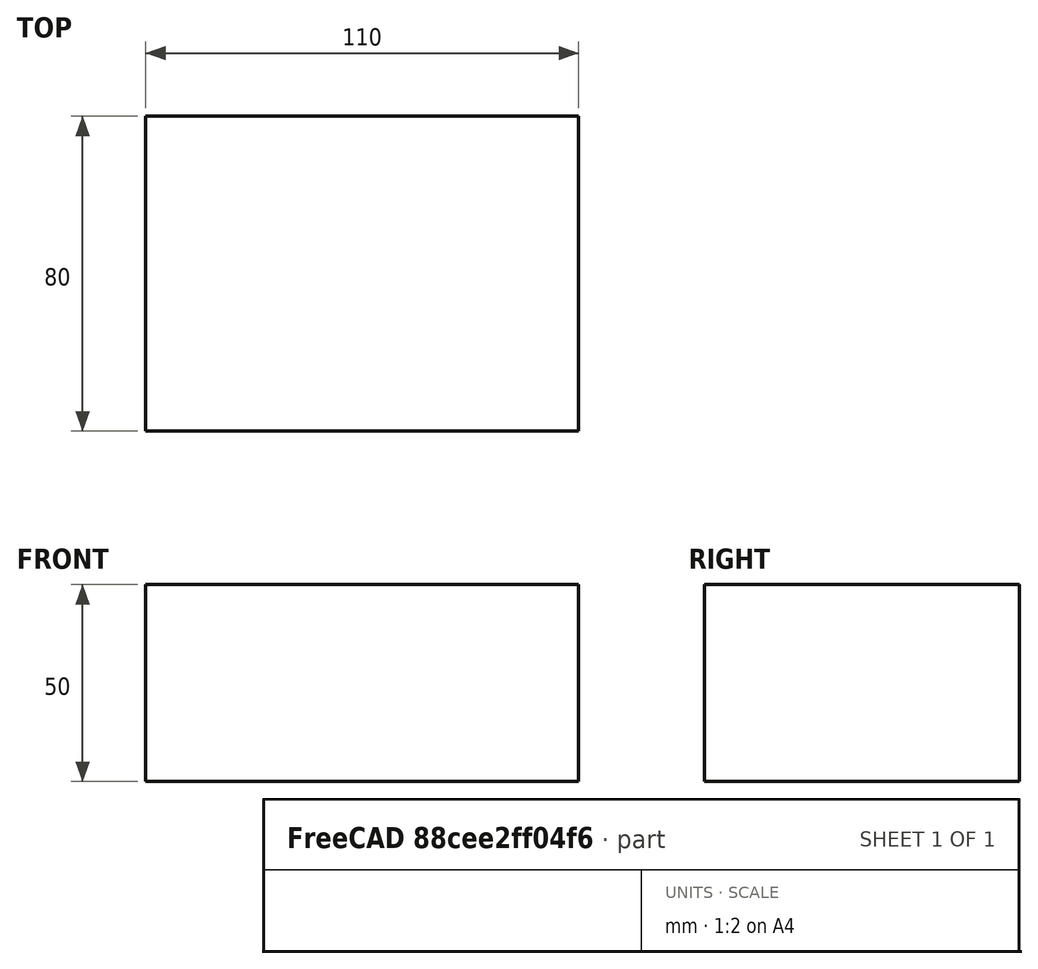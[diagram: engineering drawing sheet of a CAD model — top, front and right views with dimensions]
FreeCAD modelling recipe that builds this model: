
FCSTD DOCUMENT  (FreeCAD 0.18R16146 (Git))
Label: virtual_wall_fc-paso 3
License: All rights reserved
LicenseURL: http://en.wikipedia.org/wiki/All_rights_reserved
objects: Sketcher::SketchObject×2, PartDesign::Pad×1, PartDesign::Body×1
note: 5 computed .brp shape members not serialized (recipe doc carries the construction recipe); baked Part::Feature solids carry a one-line shape summary decoded from their .brp

FEATURE [Sketcher::SketchObject] Sketch
  MapMode = 5
  Support = -> [XY_Plane]
  sketch-geometry (4):
    g0: LineSegment StartX=0 StartY=0 StartZ=0 EndX=110 EndY=0 EndZ=0
    g1: LineSegment StartX=110 StartY=0 StartZ=0 EndX=110 EndY=80 EndZ=0
    g2: LineSegment StartX=110 StartY=80 StartZ=0 EndX=0 EndY=80 EndZ=0
    g3: LineSegment StartX=0 StartY=80 StartZ=0 EndX=0 EndY=0 EndZ=0
  constraints (11):
    c: Coincident(g0,g1)
    c: Coincident(g1,g2)
    c: Coincident(g2,g3)
    c: Coincident(g3,g0)
    c: Horizontal(g0)
    c: Horizontal(g2)
    c: Vertical(g1)
    c: Vertical(g3)
    c: Coincident(g0,g-1)
    c: DistanceX(g2,g2) = 110
    c: DistanceY(g1,g1) = 80
FEATURE [PartDesign::Pad] Pad
  Length = 50
  Length2 = 100
  Profile = -> Sketch
  Type = 0
FEATURE [Sketcher::SketchObject] Sketch001
  MapMode = 5
  Placement = pos=(0,0,50) rot=(0,0,1;0rad)
  Support = -> [Pad]
  sketch-geometry (17):
    g0: LineSegment StartX=2 StartY=10 StartZ=0 EndX=10 EndY=10 EndZ=0
    g1: LineSegment StartX=10 StartY=10 StartZ=0 EndX=10 EndY=2 EndZ=0
    g2: LineSegment StartX=10 StartY=2 StartZ=0 EndX=100 EndY=2 EndZ=0
    g3: LineSegment StartX=100 StartY=2 StartZ=0 EndX=100 EndY=10 EndZ=0
    g4: LineSegment StartX=100 StartY=10 StartZ=0 EndX=108 EndY=10 EndZ=0
    g5: LineSegment StartX=108 StartY=10 StartZ=0 EndX=108 EndY=70 EndZ=0
    g6: LineSegment StartX=108 StartY=70 StartZ=0 EndX=100 EndY=70 EndZ=0
    g7: LineSegment StartX=100 StartY=70 StartZ=0 EndX=100 EndY=78 EndZ=0
    g8: LineSegment StartX=100 StartY=78 StartZ=0 EndX=10 EndY=78 EndZ=0
    g9: LineSegment StartX=10 StartY=78 StartZ=0 EndX=10 EndY=70 EndZ=0
    g10: LineSegment StartX=10 StartY=70 StartZ=0 EndX=2 EndY=70 EndZ=0
    g11: LineSegment StartX=2 StartY=70 StartZ=0 EndX=2 EndY=10 EndZ=0
    g12: GeomPoint X=0 Y=0 Z=0
    g13: Circle CenterX=6 CenterY=74 CenterZ=0 NormalX=0 NormalY=0 NormalZ=1 AngleXU=0 Radius=1.9
    g14: Circle CenterX=104 CenterY=74 CenterZ=0 NormalX=0 NormalY=0 NormalZ=1 AngleXU=0 Radius=1.9
    g15: Circle CenterX=104 CenterY=6 CenterZ=0 NormalX=0 NormalY=0 NormalZ=1 AngleXU=0 Radius=1.9
    g16: Circle CenterX=6 CenterY=6 CenterZ=0 NormalX=0 NormalY=0 NormalZ=1 AngleXU=0 Radius=1.9
  constraints (49):
    c: Horizontal(g0)
    c: Coincident(g0,g1)
    c: Vertical(g1)
    c: Coincident(g1,g2)
    c: Horizontal(g2)
    c: Coincident(g2,g3)
    c: Coincident(g3,g4)
    c: Horizontal(g4)
    c: Coincident(g4,g5)
    c: Vertical(g5)
    c: Coincident(g5,g6)
    c: Horizontal(g6)
    c: Coincident(g6,g7)
    c: Coincident(g7,g8)
    c: Horizontal(g8)
    c: Coincident(g8,g9)
    c: Coincident(g9,g10)
    c: Coincident(g10,g11)
    c: Coincident(g11,g0)
    c: Vertical(g11)
    c: Vertical(g9)
    c: Vertical(g7)
    c: Vertical(g3)
    c: Horizontal(g10)
    c: DistanceX(g-1,g0) = 2
    c: DistanceY(g-1,g1) = 2
    c: DistanceX(g0,g0) = 8
    c: DistanceY(g1,g1) = 8
    c: DistanceX(g10,g10) = 8
    c: DistanceY(g9,g9) = 8
    c: Coincident(g12,g-1)
    c: DistanceY(g11,g11) = 60
    c: DistanceX(g8,g7) = 90
    c: DistanceY(g7,g7) = 8
    c: DistanceX(g6,g6) = 8
    c: DistanceY(g5,g5) = 60
    c: DistanceX(g4,g4) = 8
    c: DistanceX(g13,g8) = 4
    c: DistanceY(g9,g13) = 4
    c: Radius(g13) = 1.9
    c: DistanceX(g6,g14) = 4
    c: DistanceY(g6,g14) = 4
    c: Radius(g14) = 1.9
    c: DistanceX(g15,g4) = 4
    c: DistanceY(g2,g15) = 4
    c: Radius(g15) = 1.9
    c: DistanceX(g16,g1) = 4
    c: DistanceY(g16,g0) = 4
    c: Radius(g16) = 1.9
FEATURE [PartDesign::Body] Body
  Group = -> [Sketch,Pad,Sketch001]
  Origin = -> Origin
  Tip = -> Pad
